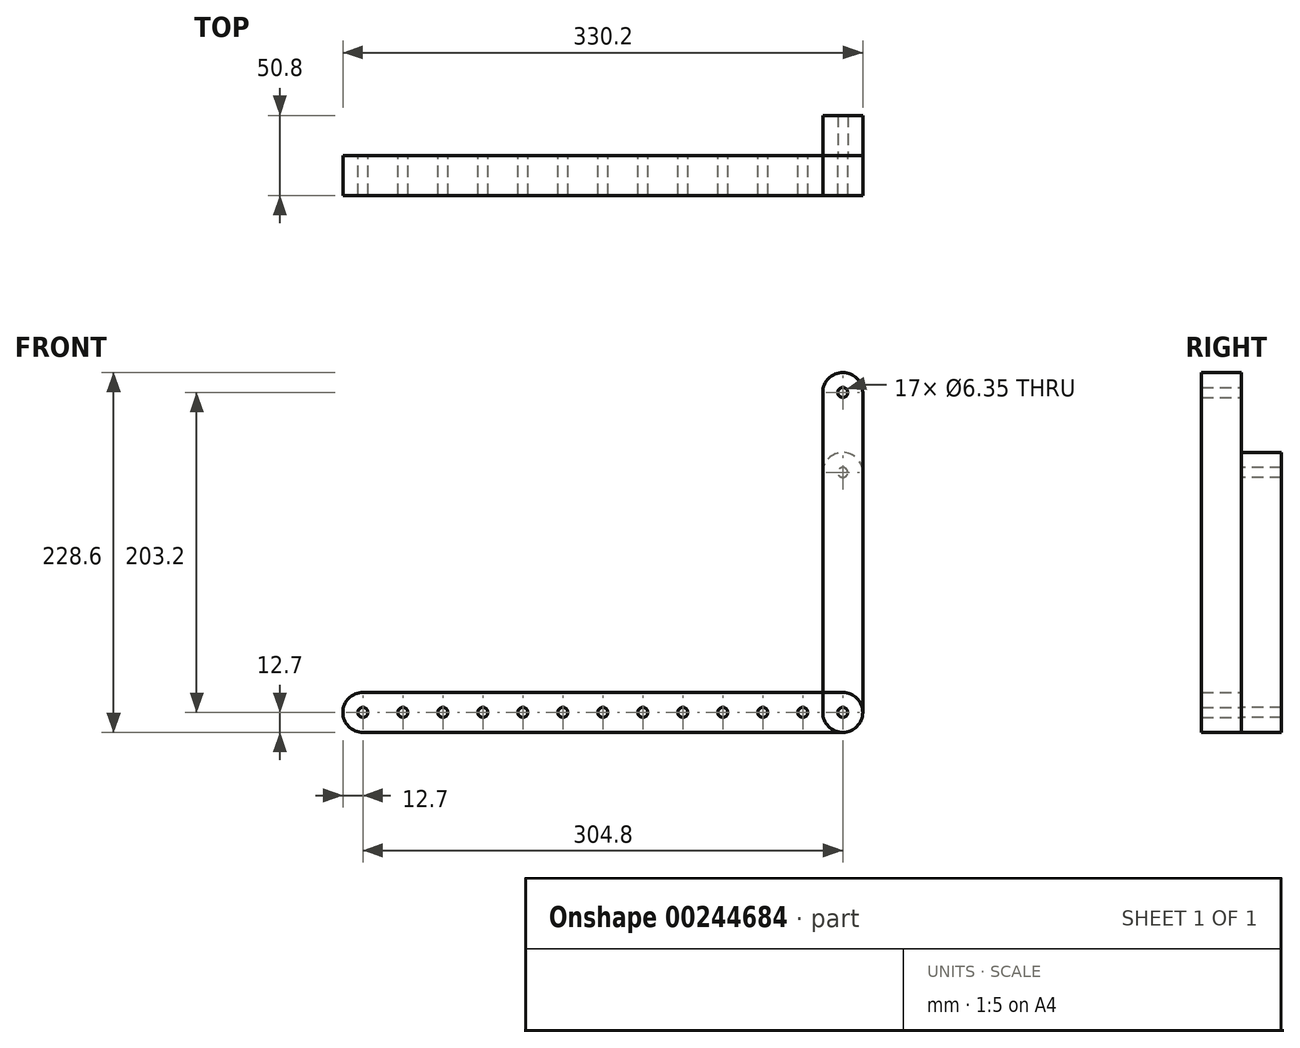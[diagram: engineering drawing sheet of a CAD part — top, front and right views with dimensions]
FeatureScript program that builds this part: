
annotation { "Feature Type Name" : "Feature", "Feature Type Description" : "" }
export const myFeature = defineFeature(function(context is Context, id is Id, definition is map)
    precondition{}
    {
        {
            var Q0;
            Q0=qCreatedBy(makeId("Front.planeOp"),FACE);
            var sketch = newSketch(context, id + "F0", { "sketchPlane" : qUnion([Q0])});
            skLineSegment(sketch, "E0.bottom", {"start": v(-12.7, 0) * mm, "end": v(12.7, 0) * mm});
            skLineSegment(sketch, "E0.top", {"start": v(-12.7, 203.2) * mm, "end": v(12.7, 203.2) * mm});
            skLineSegment(sketch, "E0.left", {"start": v(-12.7, 0) * mm, "end": v(-12.7, 203.2) * mm});
            skLineSegment(sketch, "E0.right", {"start": v(12.7, 0) * mm, "end": v(12.7, 203.2) * mm});
            skPoint(sketch, "E1", {"position": v(0, 0) * mm});
            skArc(sketch, "E2", {"start": v(-12.7, 0) * mm, "mid": v(0, -12.7) * mm, "end": v(12.7, 0) * mm});
            skArc(sketch, "E3", {"start": v(12.7, 203.2) * mm, "mid": v(0, 215.9) * mm, "end": v(-12.7, 203.2) * mm});
            skCircle(sketch, "E4", {"center": v(0, 203.2) * mm, "radius": 3.18 * mm});
            skCircle(sketch, "E5", {"center": v(0, 0) * mm, "radius": 3.17 * mm});
            skSolve(sketch);
        }
        {
            var Q0;
            Q0 = qSketchRegion(id + "F0", true);
            extrude(context, id + "F1", {"entities" : qUnion([Q0]), "depth" : 25.4 * mm, "offsetDistance" : 25.4 * mm});
        }
        {
            var Q0;
            Q0=qCreatedBy(makeId("Front.planeOp"),FACE);
            var sketch = newSketch(context, id + "F2", { "sketchPlane" : qUnion([Q0])});
            skLineSegment(sketch, "E6.bottom", {"start": v(-12.7, 0) * mm, "end": v(12.7, 0) * mm});
            skLineSegment(sketch, "E6.top", {"start": v(-12.7, 152.4) * mm, "end": v(12.7, 152.4) * mm});
            skLineSegment(sketch, "E6.left", {"start": v(-12.7, 0) * mm, "end": v(-12.7, 152.4) * mm});
            skLineSegment(sketch, "E6.right", {"start": v(12.7, 0) * mm, "end": v(12.7, 152.4) * mm});
            skArc(sketch, "E7", {"start": v(-12.7, 0) * mm, "mid": v(0, -12.7) * mm, "end": v(12.7, 0) * mm});
            skArc(sketch, "E8", {"start": v(12.7, 152.4) * mm, "mid": v(0, 165.1) * mm, "end": v(-12.7, 152.4) * mm});
            skCircle(sketch, "E9", {"center": v(0, 0) * mm, "radius": 3.17 * mm});
            skCircle(sketch, "E10", {"center": v(0, 152.4) * mm, "radius": 3.17 * mm});
            skSolve(sketch);
        }
        {
            var Q0;
            Q0 = qSketchRegion(id + "F2", true);
            extrude(context, id + "F3", {"entities" : qUnion([Q0]), "oppositeDirection" : true, "depth" : 25.4 * mm, "offsetDistance" : 25.4 * mm});
        }
        {
            var Q0;
            Q0=qCreatedBy(makeId("Front.planeOp"),FACE);
            var sketch = newSketch(context, id + "F4", { "sketchPlane" : qUnion([Q0])});
            skLineSegment(sketch, "E11.bottom", {"start": v(0, 12.7) * mm, "end": v(-304.8, 12.7) * mm});
            skLineSegment(sketch, "E11.top", {"start": v(0, -12.7) * mm, "end": v(-304.8, -12.7) * mm});
            skLineSegment(sketch, "E11.left", {"start": v(0, 12.7) * mm, "end": v(0, -12.7) * mm});
            skLineSegment(sketch, "E11.right", {"start": v(-304.8, 12.7) * mm, "end": v(-304.8, -12.7) * mm});
            skPoint(sketch, "E12", {"position": v(0, 0) * mm});
            skArc(sketch, "E13", {"start": v(0, -12.7) * mm, "mid": v(12.7, 0) * mm, "end": v(0, 12.7) * mm});
            skArc(sketch, "E14", {"start": v(-304.8, 12.7) * mm, "mid": v(-317.5, 0) * mm, "end": v(-304.8, -12.7) * mm});
            skCircle(sketch, "E15", {"center": v(0, 0) * mm, "radius": 3.17 * mm});
            skCircle(sketch, "E16", {"center": v(-304.8, 0) * mm, "radius": 3.17 * mm});
            skLineSegment(sketch, "E17", {"start": v(0, 0) * mm, "end": v(-304.8, 0) * mm, "construction": true});
            skCircle(sketch, "E18.1.0.0", {"center": v(-25.4, 0) * mm, "radius": 3.17 * mm});
            skCircle(sketch, "E18.2.0.0", {"center": v(-50.8, 0) * mm, "radius": 3.17 * mm});
            skCircle(sketch, "E18.3.0.0", {"center": v(-76.2, 0) * mm, "radius": 3.17 * mm});
            skCircle(sketch, "E18.4.0.0", {"center": v(-101.6, 0) * mm, "radius": 3.17 * mm});
            skCircle(sketch, "E18.5.0.0", {"center": v(-127, 0) * mm, "radius": 3.17 * mm});
            skCircle(sketch, "E18.6.0.0", {"center": v(-152.4, 0) * mm, "radius": 3.17 * mm});
            skCircle(sketch, "E18.7.0.0", {"center": v(-177.8, 0) * mm, "radius": 3.17 * mm});
            skCircle(sketch, "E18.8.0.0", {"center": v(-203.2, 0) * mm, "radius": 3.17 * mm});
            skCircle(sketch, "E18.9.0.0", {"center": v(-228.6, 0) * mm, "radius": 3.17 * mm});
            skCircle(sketch, "E18.10.0.0", {"center": v(-254, 0) * mm, "radius": 3.17 * mm});
            skCircle(sketch, "E18.11.0.0", {"center": v(-279.4, 0) * mm, "radius": 3.17 * mm});
            skLineSegment(sketch, "E18.direction1", {"start": v(0, 0) * mm, "end": v(-25.4, 0) * mm, "construction": true});
            skSolve(sketch);
        }
        {
            var Q0;
            Q0 = qSketchRegion(id + "F4", true);
            extrude(context, id + "F5", {"entities" : qUnion([Q0]), "depth" : 25.4 * mm, "offsetDistance" : 25.4 * mm});
        }
    });
